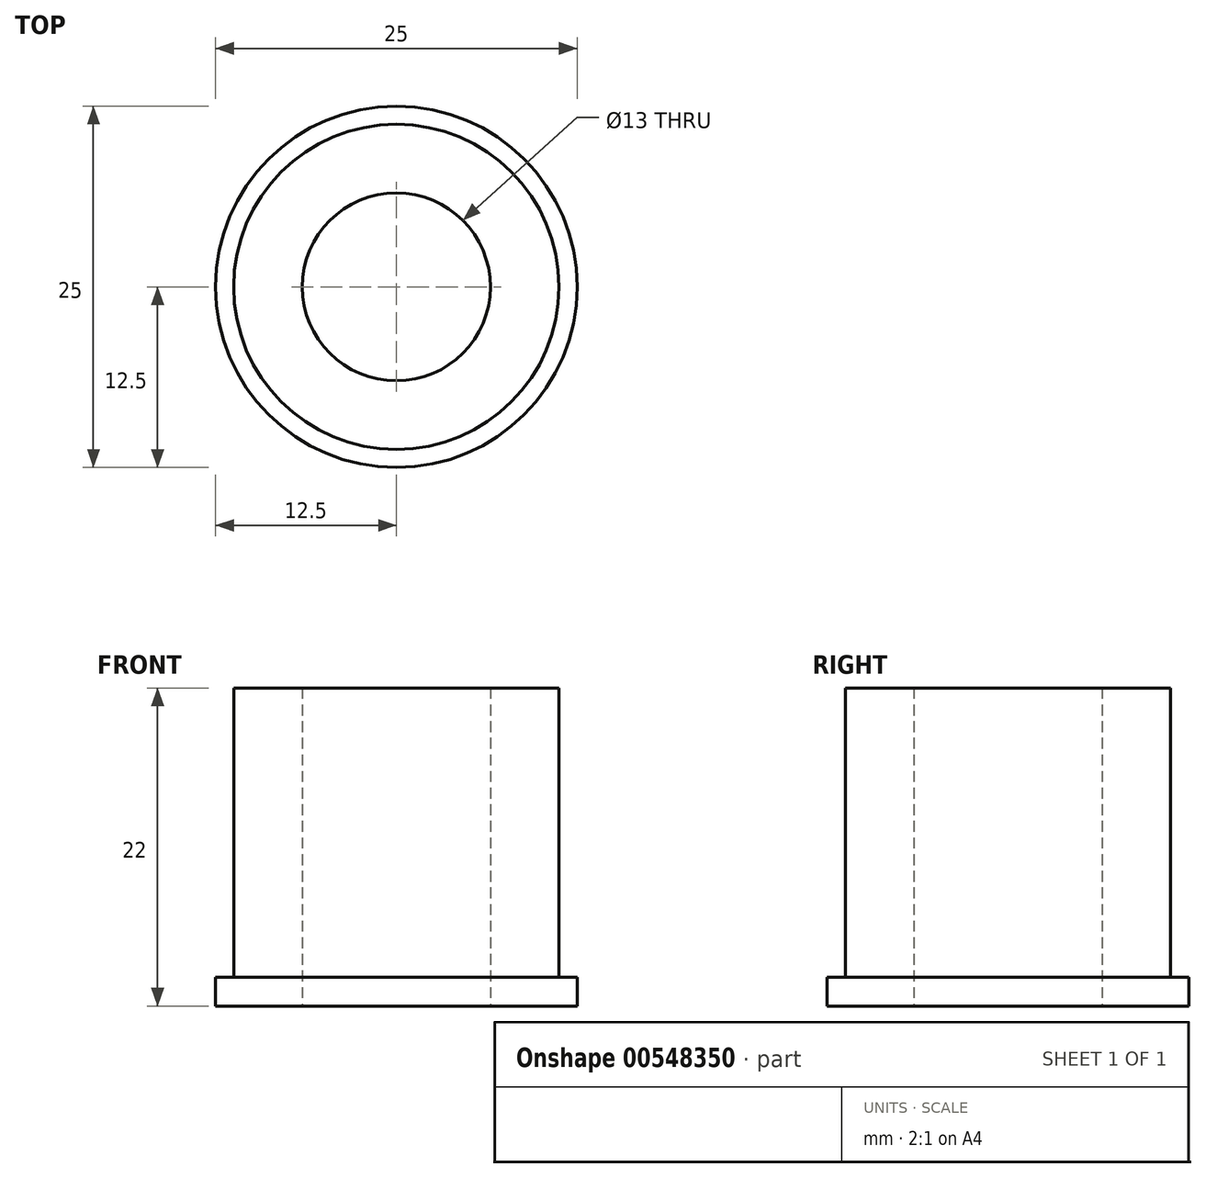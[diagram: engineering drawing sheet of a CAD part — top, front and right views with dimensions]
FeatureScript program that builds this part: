
annotation { "Feature Type Name" : "Feature", "Feature Type Description" : "" }
export const myFeature = defineFeature(function(context is Context, id is Id, definition is map)
    precondition{}
    {
        {
            var Q0;
            Q0=qCreatedBy(makeId("Top.planeOp"),FACE);
            var sketch = newSketch(context, id + "F0", { "sketchPlane" : qUnion([Q0])});
            skCircle(sketch, "E0", {"center": v(0, 0) * mm, "radius": 11.25 * mm});
            skCircle(sketch, "E1", {"center": v(0, 0) * mm, "radius": 6.5 * mm});
            skCircle(sketch, "E2", {"center": v(0, 0) * mm, "radius": 12.5 * mm});
            skSolve(sketch);
        }
        {
            var Q0;
            Q0=makeQuery(id+"F0.imprint","IMPRINT",FACE,{"disambiguationData":[TD([[makeQuery(id+"F0.imprint","IMPRINT",EDGE,{"derivedFrom":sQuery(id+"F0.wireOp",EDGE,"E0")}),1.0]])]});
            extrude(context, id + "F1", {"entities" : qUnion([Q0]), "depth" : 22 * mm, "offsetDistance" : 25 * mm});
        }
        {
            var Q0;
            Q0=qSketchRegion(id+"F0",true);
            extrude(context, id + "F2", {"entities" : qUnion([Q0]), "operationType" : NewBodyOperationType.ADD, "depth" : 2 * mm, "offsetDistance" : 25 * mm});
        }
    });
